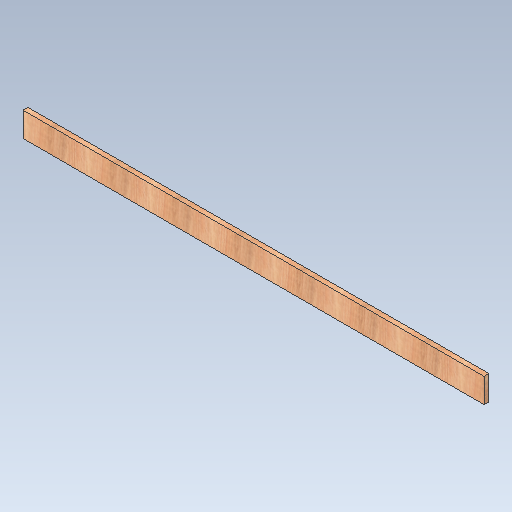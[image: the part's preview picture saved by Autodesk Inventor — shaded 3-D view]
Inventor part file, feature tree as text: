
AUTODESK INVENTOR PART (.ipt)
format: ipt  version: 2020.1 (Build 241239000, 239)  size: 124,416 bytes
history: native  units: mm
features: extrude x1, sketch x1
ambient origin geometry x8: Origin, YZ Plane, XZ Plane, XY Plane, X Axis, Y Axis, Z Axis, Center Point
bodies: Solid1 (feature_tree)
feature tree (2):
  extrude  "Extrusion1"  Depth=100.0mm
  sketch  "Sketch1"  dims[d0=1884.0mm d1=100.0mm d2=20.0mm d3=0.0mm]
